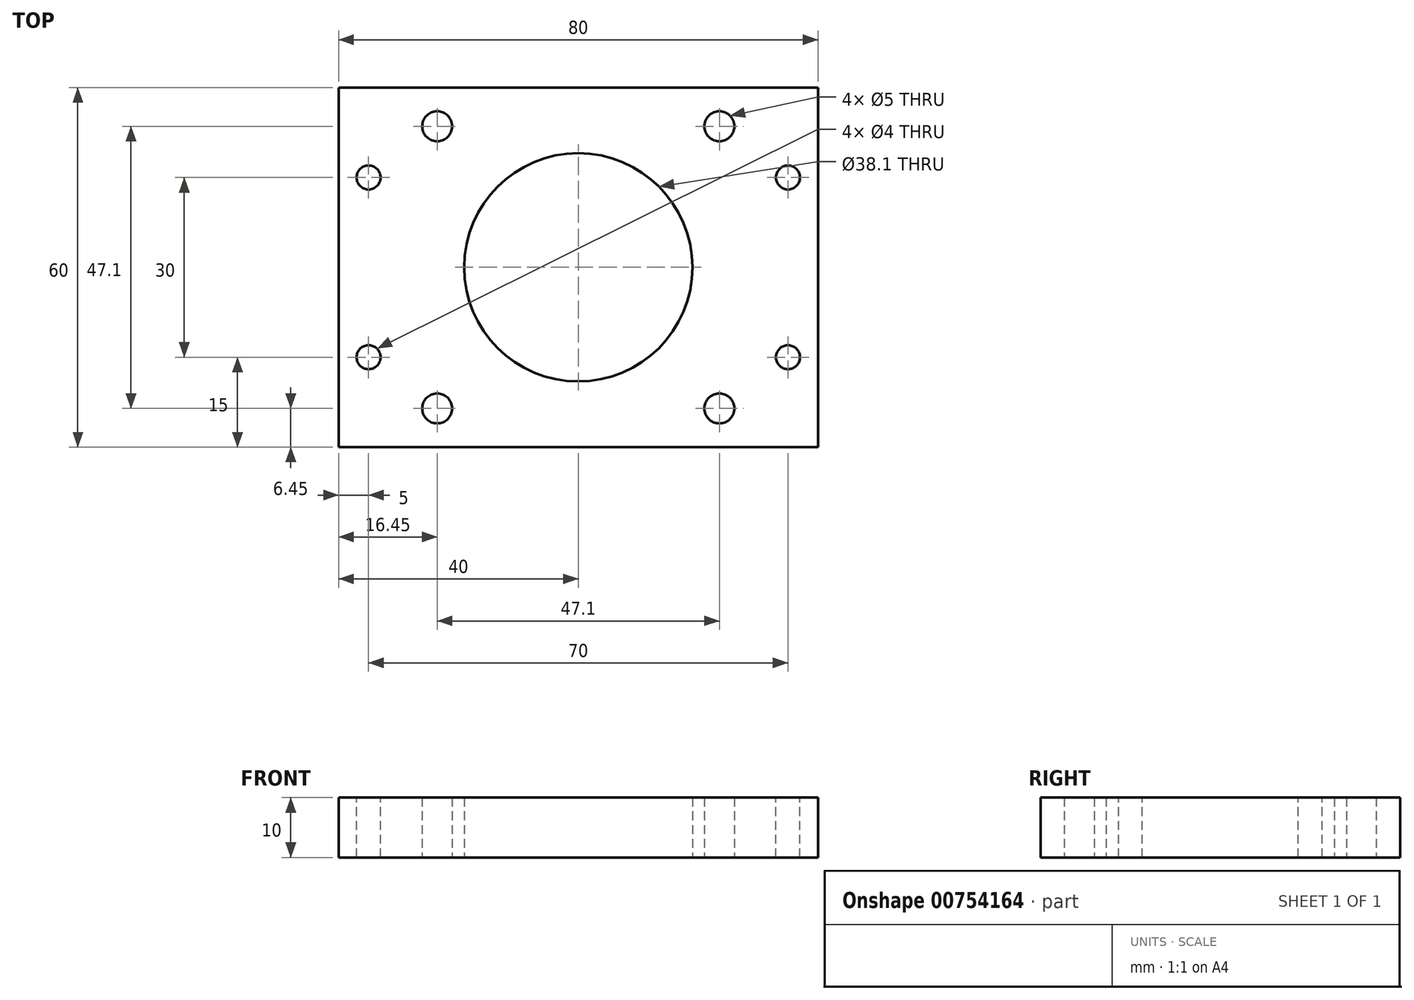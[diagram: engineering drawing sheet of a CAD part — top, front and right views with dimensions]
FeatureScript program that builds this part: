
annotation { "Feature Type Name" : "Feature", "Feature Type Description" : "" }
export const myFeature = defineFeature(function(context is Context, id is Id, definition is map)
    precondition{}
    {
        {
            var Q0;
            Q0=qCreatedBy(makeId("Top.planeOp"),FACE);
            var sketch = newSketch(context, id + "F0", { "sketchPlane" : qUnion([Q0])});
            skLineSegment(sketch, "E0.bottom", {"start": v(0, 0) * mm, "end": v(80, 0) * mm});
            skLineSegment(sketch, "E0.top", {"start": v(0, 60) * mm, "end": v(80, 60) * mm});
            skLineSegment(sketch, "E0.left", {"start": v(0, 0) * mm, "end": v(0, 60) * mm});
            skLineSegment(sketch, "E0.right", {"start": v(80, 0) * mm, "end": v(80, 60) * mm});
            skSolve(sketch);
        }
        {
            var Q0;
            Q0=makeQuery(id+"F0.imprint","IMPRINT",FACE,{"disambiguationData":[TD([[makeQuery(id+"F0.imprint","IMPRINT",EDGE,{"derivedFrom":sQuery(id+"F0.wireOp",EDGE,"E0.bottom")}),1.0]])]});
            extrude(context, id + "F1", {"entities" : qUnion([Q0]), "depth" : 10 * mm, "offsetDistance" : 25 * mm});
        }
        {
            var Q0;
            Q0=qCreatedBy(makeId("Top.planeOp"),FACE);
            var sketch = newSketch(context, id + "F2", { "sketchPlane" : qUnion([Q0])});
            skCircle(sketch, "E1", {"center": v(40, 30) * mm, "radius": 19.05 * mm});
            skSolve(sketch);
        }
        {
            var Q0;
            Q0=sQuery(id+"F2.wireOp",VERTEX,"E1.center");
            var Q1;
            Q1=makeQuery(id+"F1.opExtrude","SWEPT_BODY",BODY,{"disambiguationData":[OSD([sQuery(id+"F0.wireOp",EDGE,"E0.bottom"),sQuery(id+"F0.wireOp",EDGE,"E0.top"),sQuery(id+"F0.wireOp",EDGE,"E0.left"),sQuery(id+"F0.wireOp",EDGE,"E0.right")])]});
            hole(context, id + "F3", {"style" : HoleStyle.SIMPLE, "endStyle" : HoleEndStyle.THROUGH, "oppositeDirection" : true, "holeDiameter" : 38.1 * mm, "majorDiameter" : 5 * mm, "isTappedThrough" : true, "tappedDepth" : 12 * mm, "tapClearance" : 3, "startFromSketch" : true, "locations" : qUnion([Q0]), "scope" : qUnion([Q1])});
        }
        {
            var Q0;
            Q0=makeQuery(id+"F0.imprint","IMPRINT",FACE,{"disambiguationData":[TD([[makeQuery(id+"F0.imprint","IMPRINT",EDGE,{"derivedFrom":sQuery(id+"F0.wireOp",EDGE,"E0.bottom")}),1.0]])]});
            var sketch = newSketch(context, id + "F4", { "sketchPlane" : qUnion([Q0])});
            skPoint(sketch, "E2", {"position": v(16.45, 53.55) * mm});
            skPoint(sketch, "E3", {"position": v(63.55, 53.55) * mm});
            skPoint(sketch, "E4", {"position": v(63.55, 6.45) * mm});
            skPoint(sketch, "E5", {"position": v(16.45, 6.45) * mm});
            skSolve(sketch);
        }
        {
            var Q0;
            Q0=sQuery(id+"F4.wireOp",VERTEX,"E5");
            var Q1;
            Q1=sQuery(id+"F4.wireOp",VERTEX,"E4");
            var Q2;
            Q2=sQuery(id+"F4.wireOp",VERTEX,"E3");
            var Q3;
            Q3=sQuery(id+"F4.wireOp",VERTEX,"E2");
            var Q4;
            Q4=makeQuery(id+"F1.opExtrude","SWEPT_BODY",BODY,{"disambiguationData":[OSD([sQuery(id+"F0.wireOp",EDGE,"E0.bottom"),sQuery(id+"F0.wireOp",EDGE,"E0.top"),sQuery(id+"F0.wireOp",EDGE,"E0.left"),sQuery(id+"F0.wireOp",EDGE,"E0.right")])]});
            hole(context, id + "F5", {"style" : HoleStyle.SIMPLE, "endStyle" : HoleEndStyle.THROUGH, "oppositeDirection" : true, "holeDiameter" : 5 * mm, "majorDiameter" : 5 * mm, "isTappedThrough" : true, "tappedDepth" : 12 * mm, "tapClearance" : 3, "startFromSketch" : true, "locations" : qUnion([Q0, Q1, Q2, Q3]), "scope" : qUnion([Q4])});
        }
        {
            var Q0;
            Q0=makeQuery(id+"F1.opExtrude","CAP_FACE",FACE,{"disambiguationData":[OSD([sQuery(id+"F0.wireOp",EDGE,"E0.bottom"),sQuery(id+"F0.wireOp",EDGE,"E0.top"),sQuery(id+"F0.wireOp",EDGE,"E0.left"),sQuery(id+"F0.wireOp",EDGE,"E0.right")])],"isStart":false});
            var sketch = newSketch(context, id + "F6", { "sketchPlane" : qUnion([Q0])});
            skPoint(sketch, "E6", {"position": v(5, 15) * mm});
            skPoint(sketch, "E7", {"position": v(75, 15) * mm});
            skPoint(sketch, "E8", {"position": v(5, 45) * mm});
            skPoint(sketch, "E9", {"position": v(75, 45) * mm});
            skSolve(sketch);
        }
        {
            var Q0;
            Q0=sQuery(id+"F6.wireOp",VERTEX,"E8");
            var Q1;
            Q1=sQuery(id+"F6.wireOp",VERTEX,"E9");
            var Q2;
            Q2=sQuery(id+"F6.wireOp",VERTEX,"E7");
            var Q3;
            Q3=sQuery(id+"F6.wireOp",VERTEX,"E6");
            var Q4;
            Q4=makeQuery(id+"F1.opExtrude","SWEPT_BODY",BODY,{"disambiguationData":[OSD([sQuery(id+"F0.wireOp",EDGE,"E0.bottom"),sQuery(id+"F0.wireOp",EDGE,"E0.top"),sQuery(id+"F0.wireOp",EDGE,"E0.left"),sQuery(id+"F0.wireOp",EDGE,"E0.right")])]});
            hole(context, id + "F7", {"style" : HoleStyle.SIMPLE, "endStyle" : HoleEndStyle.THROUGH, "holeDiameter" : 4 * mm, "majorDiameter" : 5 * mm, "isTappedThrough" : true, "tappedDepth" : 12 * mm, "tapClearance" : 3, "startFromSketch" : true, "locations" : qUnion([Q0, Q1, Q2, Q3]), "scope" : qUnion([Q4])});
        }
    });
